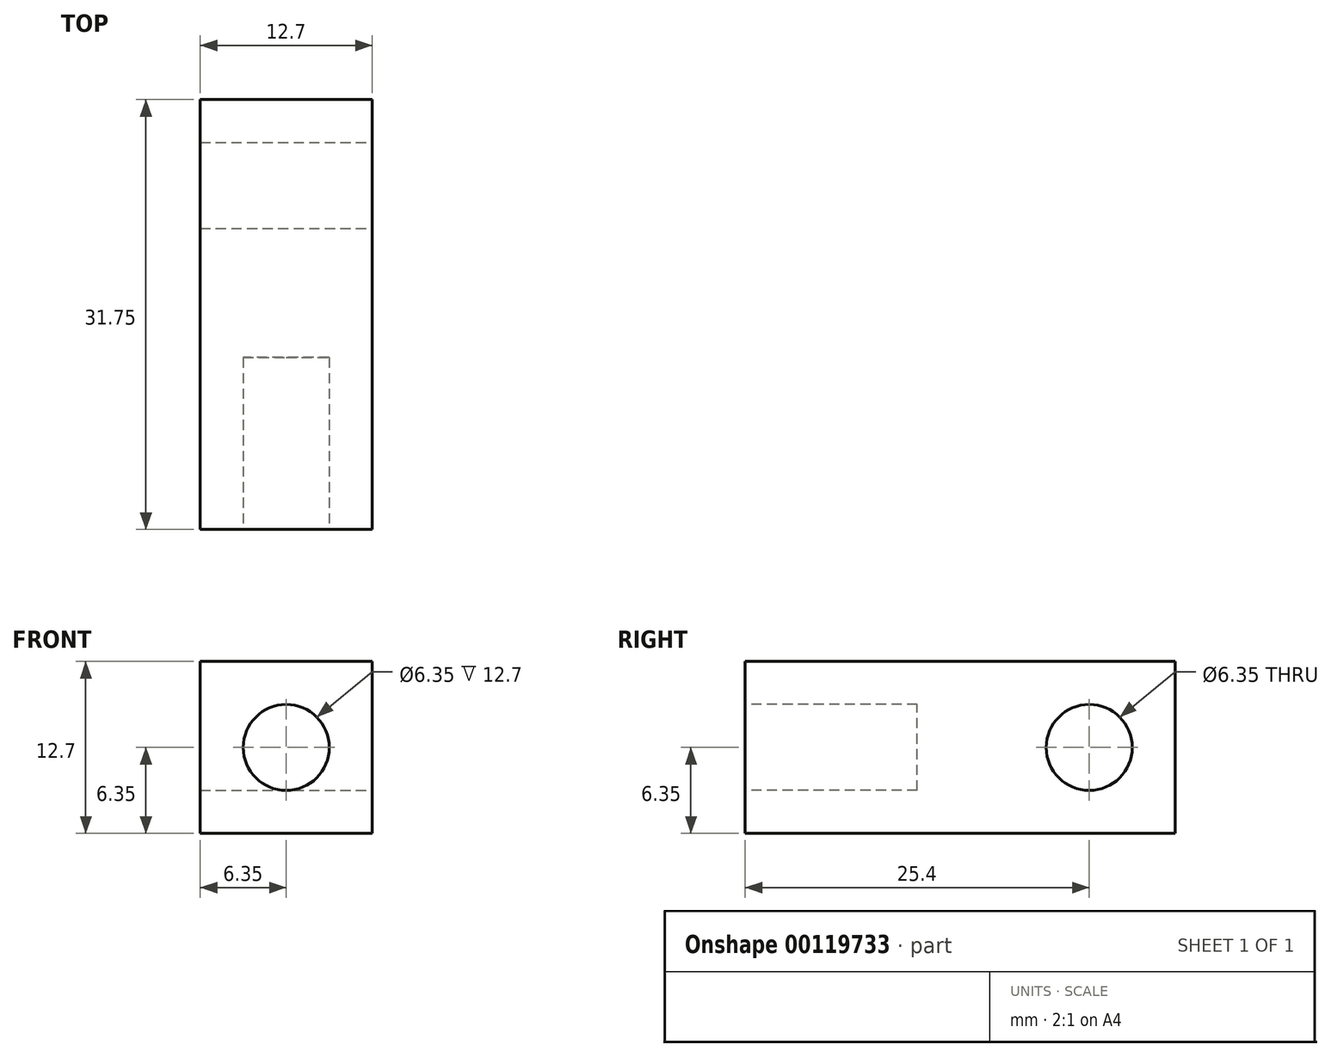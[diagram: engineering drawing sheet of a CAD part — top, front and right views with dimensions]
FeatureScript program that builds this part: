
annotation { "Feature Type Name" : "Feature", "Feature Type Description" : "" }
export const myFeature = defineFeature(function(context is Context, id is Id, definition is map)
    precondition{}
    {
        {
            var Q0;
            Q0=qCreatedBy(makeId("Front.planeOp"),FACE);
            var sketch = newSketch(context, id + "F0", { "sketchPlane" : qUnion([Q0])});
            skLineSegment(sketch, "E0.bottom", {"start": v(6.35, -6.35) * mm, "end": v(-6.35, -6.35) * mm});
            skLineSegment(sketch, "E0.top", {"start": v(6.35, 6.35) * mm, "end": v(-6.35, 6.35) * mm});
            skLineSegment(sketch, "E0.left", {"start": v(6.35, -6.35) * mm, "end": v(6.35, 6.35) * mm});
            skLineSegment(sketch, "E0.right", {"start": v(-6.35, -6.35) * mm, "end": v(-6.35, 6.35) * mm});
            skPoint(sketch, "E0.middle", {"position": v(0, 0) * mm});
            skSolve(sketch);
        }
        {
            var Q0;
            Q0=qSketchRegion(id+"F0",true);
            extrude(context, id + "F1", {"entities" : qUnion([Q0]), "oppositeDirection" : true, "depth" : 31.75 * mm});
        }
        {
            var Q0;
            Q0=makeQuery(id+"F1.opExtrude","CAP_FACE",FACE,{"disambiguationData":[OSD([sQuery(id+"F0.wireOp",EDGE,"E0.bottom"),sQuery(id+"F0.wireOp",EDGE,"E0.top"),sQuery(id+"F0.wireOp",EDGE,"E0.left"),sQuery(id+"F0.wireOp",EDGE,"E0.right")])],"isStart":true});
            var sketch = newSketch(context, id + "F2", { "sketchPlane" : qUnion([Q0])});
            skCircle(sketch, "E1", {"center": v(0, 0) * mm, "radius": 3.18 * mm});
            skSolve(sketch);
        }
        {
            var Q0;
            Q0=qSketchRegion(id+"F2",true);
            extrude(context, id + "F3", {"entities" : qUnion([Q0]), "operationType" : NewBodyOperationType.REMOVE, "oppositeDirection" : true, "depth" : 12.7 * mm});
        }
        {
            var Q0;
            Q0=makeQuery(id+"F1.opExtrude","SWEPT_FACE",FACE,{"disambiguationData":[OSD([sQuery(id+"F0.wireOp",EDGE,"E0.left")])]});
            var sketch = newSketch(context, id + "F4", { "sketchPlane" : qUnion([Q0])});
            skCircle(sketch, "E2", {"center": v(25.4, 0) * mm, "radius": 3.17 * mm});
            skPoint(sketch, "E2.centerSnap0", {"position": v(31.75, 0) * mm});
            skSolve(sketch);
        }
        {
            var Q0;
            Q0=qSketchRegion(id+"F4",true);
            extrude(context, id + "F5", {"entities" : qUnion([Q0]), "operationType" : NewBodyOperationType.REMOVE, "endBound" : BoundingType.THROUGH_ALL, "oppositeDirection" : true, "depth" : 25 * mm});
        }
    });
